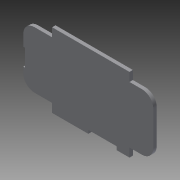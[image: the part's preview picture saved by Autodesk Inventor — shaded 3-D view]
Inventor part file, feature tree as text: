
AUTODESK INVENTOR PART (.ipt)
format: ipt  version: 2015 (Build 190159000, 159)  size: 110,080 bytes
history: native  units: mm
features: extrude x1, fillet x1, sketch x1
ambient origin geometry x8: Origin, YZ Plane, XZ Plane, XY Plane, X Axis, Y Axis, Z Axis, Center Point
bodies: Solid1 (feature_tree)
feature tree (3):
  extrude  "Extrusion1"  Depth=100.4mm
  fillet  "Fillet1"  Radius=42.2mm
  sketch  "Sketch1"  dims[d0=230.0mm d1=100.4mm d2=42.2mm d3=15.4mm d4=42.2mm d5=15.4mm d13=40.0mm d14=3.0mm d15=30.4mm d16=6.0mm d17=0.0mm d18=20.0mm d21=6.0mm]
